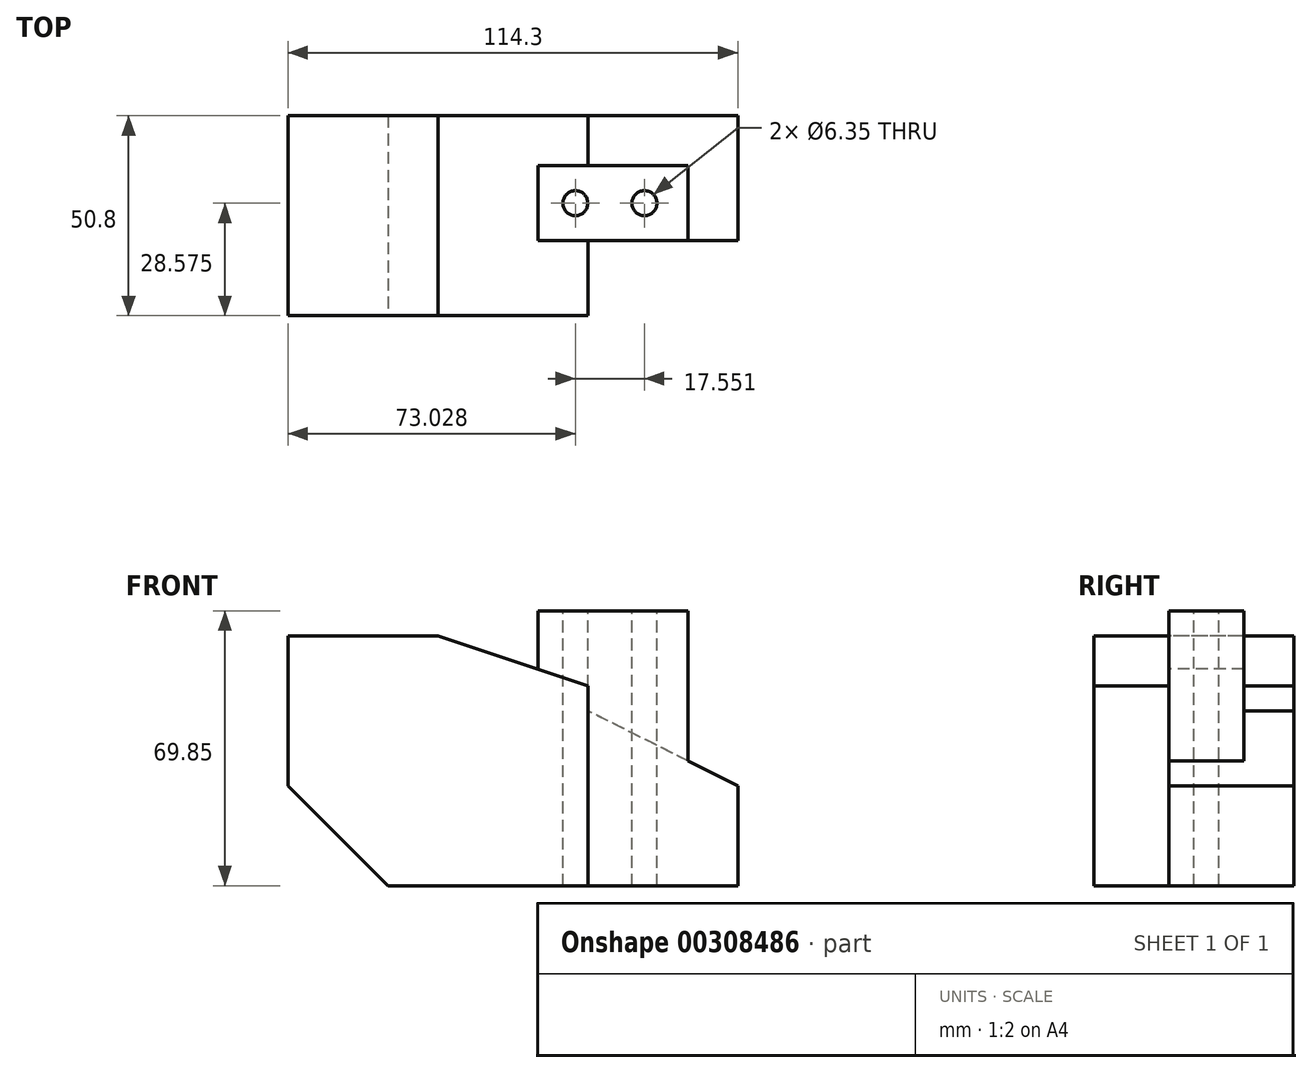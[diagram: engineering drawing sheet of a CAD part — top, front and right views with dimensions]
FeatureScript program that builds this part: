
annotation { "Feature Type Name" : "Feature", "Feature Type Description" : "" }
export const myFeature = defineFeature(function(context is Context, id is Id, definition is map)
    precondition{}
    {
        {
            var Q0;
            Q0=qCreatedBy(makeId("Front.planeOp"),FACE);
            var sketch = newSketch(context, id + "F0", { "sketchPlane" : qUnion([Q0])});
            skLineSegment(sketch, "E0", {"start": v(-45.6, 53.07) * mm, "end": v(-45.6, -10.43) * mm});
            skLineSegment(sketch, "E1", {"start": v(-45.6, -10.43) * mm, "end": v(30.6, -10.43) * mm});
            skLineSegment(sketch, "E2", {"start": v(30.6, -10.43) * mm, "end": v(30.6, 53.07) * mm});
            skLineSegment(sketch, "E3", {"start": v(30.6, 53.07) * mm, "end": v(-45.6, 53.07) * mm});
            skSolve(sketch);
        }
        {
            var Q0;
            Q0 = qSketchRegion(id + "F0", true);
            extrude(context, id + "F1", {"entities" : qUnion([Q0]), "oppositeDirection" : true, "depth" : 50.8 * mm});
        }
        {
            var Q0;
            Q0=makeQuery(id+"F1.opExtrude","CAP_FACE",FACE,{"disambiguationData":[OSD([sQuery(id+"F0.wireOp",EDGE,"E0"),sQuery(id+"F0.wireOp",EDGE,"E1"),sQuery(id+"F0.wireOp",EDGE,"E2"),sQuery(id+"F0.wireOp",EDGE,"E3")])],"isStart":true});
            var sketch = newSketch(context, id + "F2", { "sketchPlane" : qUnion([Q0])});
            skLineSegment(sketch, "E4", {"start": v(-45.6, -10.43) * mm, "end": v(-20.2, -10.43) * mm});
            skLineSegment(sketch, "E5", {"start": v(-45.6, -10.43) * mm, "end": v(-45.6, 14.97) * mm});
            skLineSegment(sketch, "E6", {"start": v(-45.6, 14.97) * mm, "end": v(-20.2, -10.43) * mm});
            skLineSegment(sketch, "E7", {"start": v(30.6, 53.07) * mm, "end": v(-7.5, 53.07) * mm});
            skLineSegment(sketch, "E8", {"start": v(30.6, 53.07) * mm, "end": v(30.6, 40.37) * mm});
            skLineSegment(sketch, "E9", {"start": v(30.6, 40.37) * mm, "end": v(-7.5, 53.07) * mm});
            skSolve(sketch);
        }
        {
            var Q0;
            Q0 = qSketchRegion(id + "F2", true);
            extrude(context, id + "F3", {"entities" : qUnion([Q0]), "operationType" : NewBodyOperationType.REMOVE, "oppositeDirection" : true, "depth" : 50.8 * mm});
        }
        {
            var Q0;
            Q0=makeQuery(id+"F1.opExtrude","SWEPT_FACE",FACE,{"disambiguationData":[OSD([sQuery(id+"F0.wireOp",EDGE,"E2")])]});
            var sketch = newSketch(context, id + "F4", { "sketchPlane" : qUnion([Q0])});
            skLineSegment(sketch, "E10", {"start": v(19.05, -10.43) * mm, "end": v(50.8, -10.43) * mm});
            skLineSegment(sketch, "E11", {"start": v(19.05, -10.43) * mm, "end": v(19.05, 14.97) * mm});
            skLineSegment(sketch, "E12", {"start": v(19.05, 14.97) * mm, "end": v(50.8, 14.97) * mm});
            skLineSegment(sketch, "E13", {"start": v(50.8, 14.97) * mm, "end": v(50.8, -10.43) * mm});
            skLineSegment(sketch, "E14", {"start": v(19.05, 14.97) * mm, "end": v(19.05, 59.42) * mm});
            skLineSegment(sketch, "E15", {"start": v(19.05, 59.42) * mm, "end": v(38.1, 59.42) * mm});
            skLineSegment(sketch, "E16", {"start": v(38.1, 59.42) * mm, "end": v(38.1, 14.97) * mm});
            skSolve(sketch);
        }
        {
            var Q0;
            Q0 = qSketchRegion(id + "F4", true);
            extrude(context, id + "F5", {"entities" : qUnion([Q0]), "operationType" : NewBodyOperationType.ADD, "depth" : 38.1 * mm});
        }
        {
            var Q0;
            Q0=makeQuery(id+"F5.opExtrude","CAP_FACE",FACE,{"disambiguationData":[OSD([sQuery(id+"F4.wireOp",EDGE,"E10"),sQuery(id+"F4.wireOp",EDGE,"E11"),sQuery(id+"F4.wireOp",EDGE,"E12"),sQuery(id+"F4.wireOp",EDGE,"E13"),sQuery(id+"F4.wireOp",EDGE,"E14"),sQuery(id+"F4.wireOp",EDGE,"E15"),sQuery(id+"F4.wireOp",EDGE,"E16")])],"isStart":true});
            var sketch = newSketch(context, id + "F6", { "sketchPlane" : qUnion([Q0])});
            skSolve(sketch);
        }
        {
            var Q0;
            Q0 = qSketchRegion(id + "F6", true);
            var Q1;
            {var subQ0=sQuery(id+"F4.wireOp",EDGE,"E15");Q1=makeQuery(id+"F6.imprint","IMPRINT",FACE,{"disambiguationData":[TD([[makeQuery(id+"F6.imprint","IMPRINT",EDGE,{"derivedFrom":makeQuery(id+"F5.opExtrude","CAP_EDGE",EDGE,{"disambiguationData":[OSD([subQ0])],"isStart":true})}),1.0]])]});}
            extrude(context, id + "F7", {"entities" : qUnion([Q0, Q1]), "operationType" : NewBodyOperationType.ADD, "depth" : 12.7 * mm});
        }
        {
            var Q0;
            {var subQ0=sQuery(id+"F4.wireOp",EDGE,"E14");var subQ1=sQuery(id+"F4.wireOp",EDGE,"E11");Q0=makeQuery(id+"F7.boolean.opBoolean","MERGE",FACE,{"derivedFrom":[makeQuery(id+"F5.opExtrude","SWEPT_FACE",FACE,{"disambiguationData":[OSD([subQ1,subQ0])]}),makeQuery(id+"F7.opExtrude","SWEPT_FACE",FACE,{"disambiguationData":[OSD([subQ1,subQ0])]})]});}
            var sketch = newSketch(context, id + "F8", { "sketchPlane" : qUnion([Q0])});
            skLineSegment(sketch, "E17", {"start": v(56, 21.32) * mm, "end": v(68.7, 14.97) * mm});
            skLineSegment(sketch, "E18", {"start": v(56, 21.32) * mm, "end": v(56, 59.42) * mm});
            skLineSegment(sketch, "E19", {"start": v(56, 59.42) * mm, "end": v(68.7, 59.42) * mm});
            skLineSegment(sketch, "E20", {"start": v(68.7, 59.42) * mm, "end": v(68.7, 14.97) * mm});
            skSolve(sketch);
        }
        {
            var Q0;
            {var subQ0=sQuery(id+"F4.wireOp",EDGE,"E16");Q0=makeQuery(id+"F7.boolean.opBoolean","MERGE",FACE,{"derivedFrom":[makeQuery(id+"F5.opExtrude","SWEPT_FACE",FACE,{"disambiguationData":[OSD([subQ0])]}),makeQuery(id+"F7.opExtrude","SWEPT_FACE",FACE,{"disambiguationData":[OSD([subQ0])]})]});}
            var sketch = newSketch(context, id + "F9", { "sketchPlane" : qUnion([Q0])});
            skLineSegment(sketch, "E21", {"start": v(-68.7, 14.97) * mm, "end": v(-30.6, 34.02) * mm});
            skLineSegment(sketch, "E22", {"start": v(-30.6, 34.02) * mm, "end": v(-30.6, 14.97) * mm});
            skLineSegment(sketch, "E23", {"start": v(-30.6, 14.97) * mm, "end": v(-68.7, 14.97) * mm});
            skSolve(sketch);
        }
        {
            var Q0;
            Q0 = qSketchRegion(id + "F9", true);
            extrude(context, id + "F10", {"entities" : qUnion([Q0]), "operationType" : NewBodyOperationType.ADD, "depth" : 12.7 * mm});
        }
        {
            var Q0;
            {var subQ0=sQuery(id+"F4.wireOp",EDGE,"E15");Q0=makeQuery(id+"F7.boolean.opBoolean","MERGE",FACE,{"derivedFrom":[makeQuery(id+"F5.opExtrude","SWEPT_FACE",FACE,{"disambiguationData":[OSD([subQ0])]}),makeQuery(id+"F7.opExtrude","SWEPT_FACE",FACE,{"disambiguationData":[OSD([subQ0])]})]});}
            var sketch = newSketch(context, id + "F11", { "sketchPlane" : qUnion([Q0])});
            skCircle(sketch, "E24", {"center": v(27.43, 28.58) * mm, "radius": 3.18 * mm});
            skPoint(sketch, "E24.centerSnap0", {"position": v(17.9, 28.58) * mm});
            skCircle(sketch, "E25", {"center": v(44.98, 28.58) * mm, "radius": 3.18 * mm});
            skPoint(sketch, "E25.centerSnap0", {"position": v(54.5, 28.58) * mm});
            skSolve(sketch);
        }
        {
            var Q0;
            Q0 = qSketchRegion(id + "F11", true);
            extrude(context, id + "F12", {"entities" : qUnion([Q0]), "operationType" : NewBodyOperationType.REMOVE, "endBound" : BoundingType.THROUGH_ALL, "oppositeDirection" : true, "depth" : 25.4 * mm});
        }
        {
            var Q0;
            Q0 = qSketchRegion(id + "F8", true);
            extrude(context, id + "F13", {"entities" : qUnion([Q0]), "operationType" : NewBodyOperationType.REMOVE, "oppositeDirection" : true, "depth" : 31.75 * mm});
        }
    });
